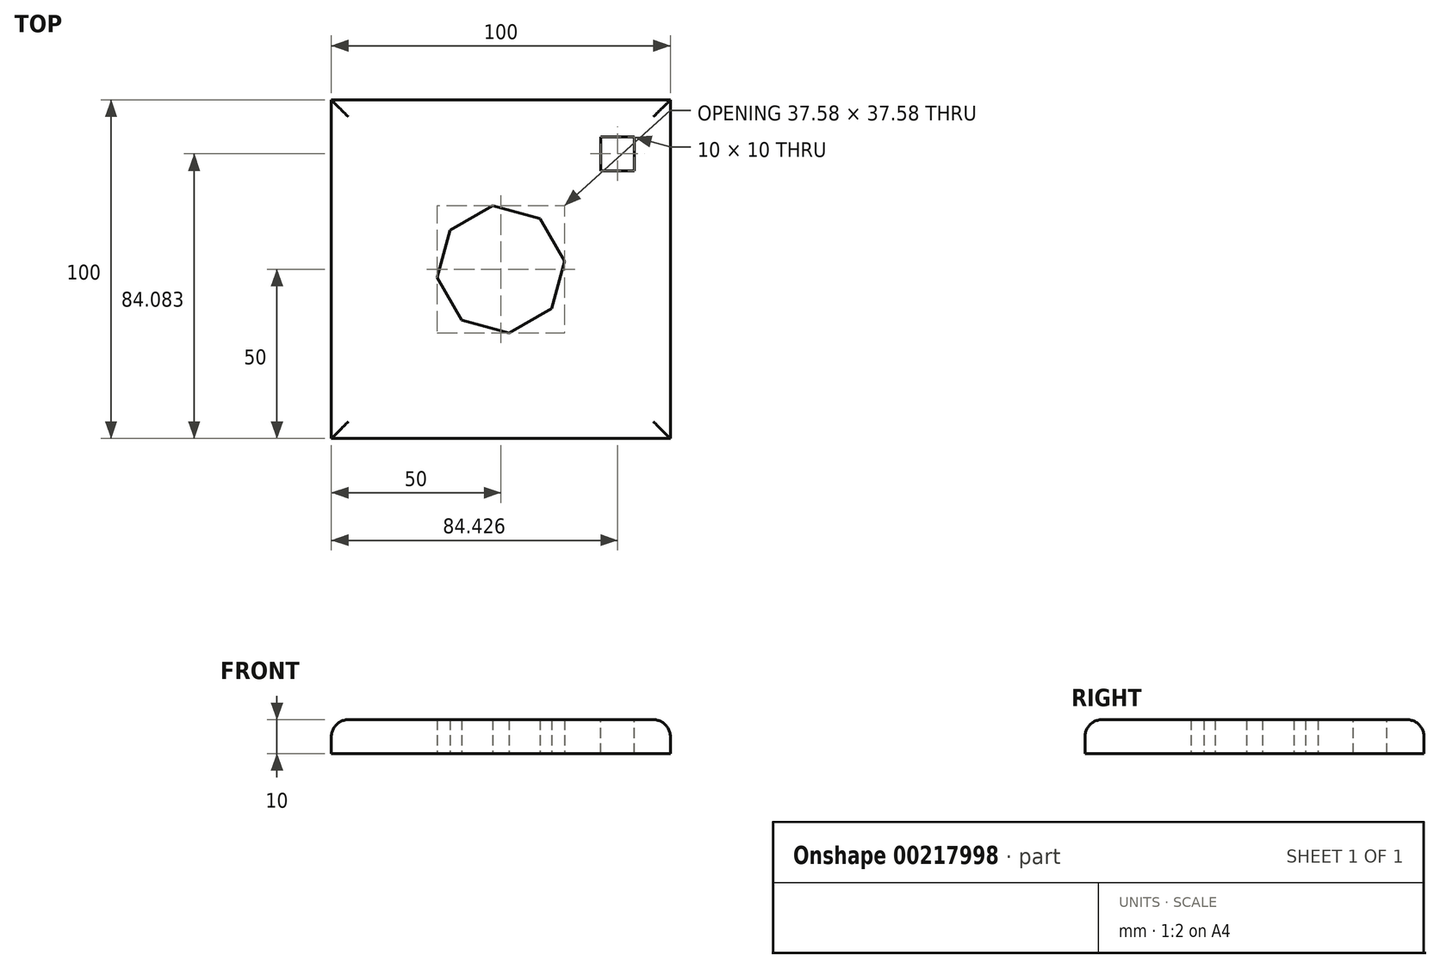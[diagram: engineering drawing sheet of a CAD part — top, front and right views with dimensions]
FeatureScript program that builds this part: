
annotation { "Feature Type Name" : "Feature", "Feature Type Description" : "" }
export const myFeature = defineFeature(function(context is Context, id is Id, definition is map)
    precondition{}
    {
        {
            var Q0;
            Q0=qCreatedBy(makeId("Top.planeOp"),FACE);
            var sketch = newSketch(context, id + "F0", { "sketchPlane" : qUnion([Q0])});
            skLineSegment(sketch, "E0.bottom", {"start": v(50, 50) * mm, "end": v(-50, 50) * mm});
            skLineSegment(sketch, "E0.top", {"start": v(50, -50) * mm, "end": v(-50, -50) * mm});
            skLineSegment(sketch, "E0.left", {"start": v(50, 50) * mm, "end": v(50, -50) * mm});
            skLineSegment(sketch, "E0.right", {"start": v(-50, 50) * mm, "end": v(-50, -50) * mm});
            skPoint(sketch, "E0.middle", {"position": v(0, 0) * mm});
            skSolve(sketch);
        }
        {
            var Q0;
            Q0=makeQuery(id+"F0.imprint","IMPRINT",FACE,{"disambiguationData":[TD([[makeQuery(id+"F0.imprint","IMPRINT",EDGE,{"derivedFrom":sQuery(id+"F0.wireOp",EDGE,"E0.bottom")}),1.0]])]});
            var sketch = newSketch(context, id + "F1", { "sketchPlane" : qUnion([Q0])});
            skCircle(sketch, "E1.cCircle", {"center": v(0, 0) * mm, "radius": 17.5 * mm, "construction": true});
            skLineSegment(sketch, "E1.0", {"start": v(11.59, 14.99) * mm, "end": v(18.79, 2.4) * mm});
            skLineSegment(sketch, "E1.1", {"start": v(18.79, 2.4) * mm, "end": v(14.99, -11.59) * mm});
            skLineSegment(sketch, "E1.2", {"start": v(14.99, -11.59) * mm, "end": v(2.4, -18.79) * mm});
            skLineSegment(sketch, "E1.3", {"start": v(2.4, -18.79) * mm, "end": v(-11.59, -14.99) * mm});
            skLineSegment(sketch, "E1.4", {"start": v(-11.59, -14.99) * mm, "end": v(-18.79, -2.4) * mm});
            skLineSegment(sketch, "E1.5", {"start": v(-18.79, -2.4) * mm, "end": v(-14.99, 11.59) * mm});
            skLineSegment(sketch, "E1.6", {"start": v(-14.99, 11.59) * mm, "end": v(-2.4, 18.79) * mm});
            skLineSegment(sketch, "E1.7", {"start": v(-2.4, 18.79) * mm, "end": v(11.59, 14.99) * mm});
            skPoint(sketch, "E1.0.midPoint", {"position": v(15.19, 8.7) * mm});
            skSolve(sketch);
        }
        {
            var Q0;
            Q0=makeQuery(id+"F0.imprint","IMPRINT",FACE,{"disambiguationData":[TD([[makeQuery(id+"F0.imprint","IMPRINT",EDGE,{"derivedFrom":sQuery(id+"F0.wireOp",EDGE,"E0.bottom")}),1.0]])]});
            extrude(context, id + "F2", {"entities" : qUnion([Q0]), "depth" : 10 * mm});
        }
        {
            var Q0;
            Q0=makeQuery(id+"F2.opExtrude","CAP_FACE",FACE,{"disambiguationData":[OSD([sQuery(id+"F0.wireOp",EDGE,"E0.bottom"),sQuery(id+"F0.wireOp",EDGE,"E0.top"),sQuery(id+"F0.wireOp",EDGE,"E0.left"),sQuery(id+"F0.wireOp",EDGE,"E0.right")])],"isStart":false});
            fillet(context, id + "F3", {"entities" : qUnion([Q0]), "radius" : 5 * mm, "tangentPropagation" : true, "allowEdgeOverflow" : false});
        }
        {
            var Q0;
            Q0=makeQuery(id+"F1.imprint","IMPRINT",FACE,{"disambiguationData":[TD([[makeQuery(id+"F1.imprint","IMPRINT",EDGE,{"derivedFrom":sQuery(id+"F1.wireOp",EDGE,"E1.0")}),-1.0]])]});
            extrude(context, id + "F4", {"entities" : qUnion([Q0]), "operationType" : NewBodyOperationType.REMOVE, "depth" : 106.8 * mm});
        }
        {
            var Q0;
            Q0=makeQuery(id+"F2.opExtrude","CAP_FACE",FACE,{"disambiguationData":[OSD([sQuery(id+"F0.wireOp",EDGE,"E0.bottom"),sQuery(id+"F0.wireOp",EDGE,"E0.top"),sQuery(id+"F0.wireOp",EDGE,"E0.left"),sQuery(id+"F0.wireOp",EDGE,"E0.right")])],"isStart":false});
            var sketch = newSketch(context, id + "F5", { "sketchPlane" : qUnion([Q0])});
            skLineSegment(sketch, "E2.bottom", {"start": v(39.43, 39.08) * mm, "end": v(29.43, 39.08) * mm});
            skLineSegment(sketch, "E2.top", {"start": v(39.43, 29.08) * mm, "end": v(29.43, 29.08) * mm});
            skLineSegment(sketch, "E2.left", {"start": v(39.43, 39.08) * mm, "end": v(39.43, 29.08) * mm});
            skLineSegment(sketch, "E2.right", {"start": v(29.43, 39.08) * mm, "end": v(29.43, 29.08) * mm});
            skPoint(sketch, "E2.middle", {"position": v(34.43, 34.08) * mm});
            skSolve(sketch);
        }
        {
            var Q0;
            Q0=makeQuery(id+"F5.imprint","IMPRINT",FACE,{"disambiguationData":[TD([[makeQuery(id+"F5.imprint","IMPRINT",EDGE,{"derivedFrom":sQuery(id+"F5.wireOp",EDGE,"E2.bottom")}),1.0]])]});
            extrude(context, id + "F6", {"entities" : qUnion([Q0]), "operationType" : NewBodyOperationType.REMOVE, "oppositeDirection" : true, "depth" : 90.6 * mm});
        }
    });
